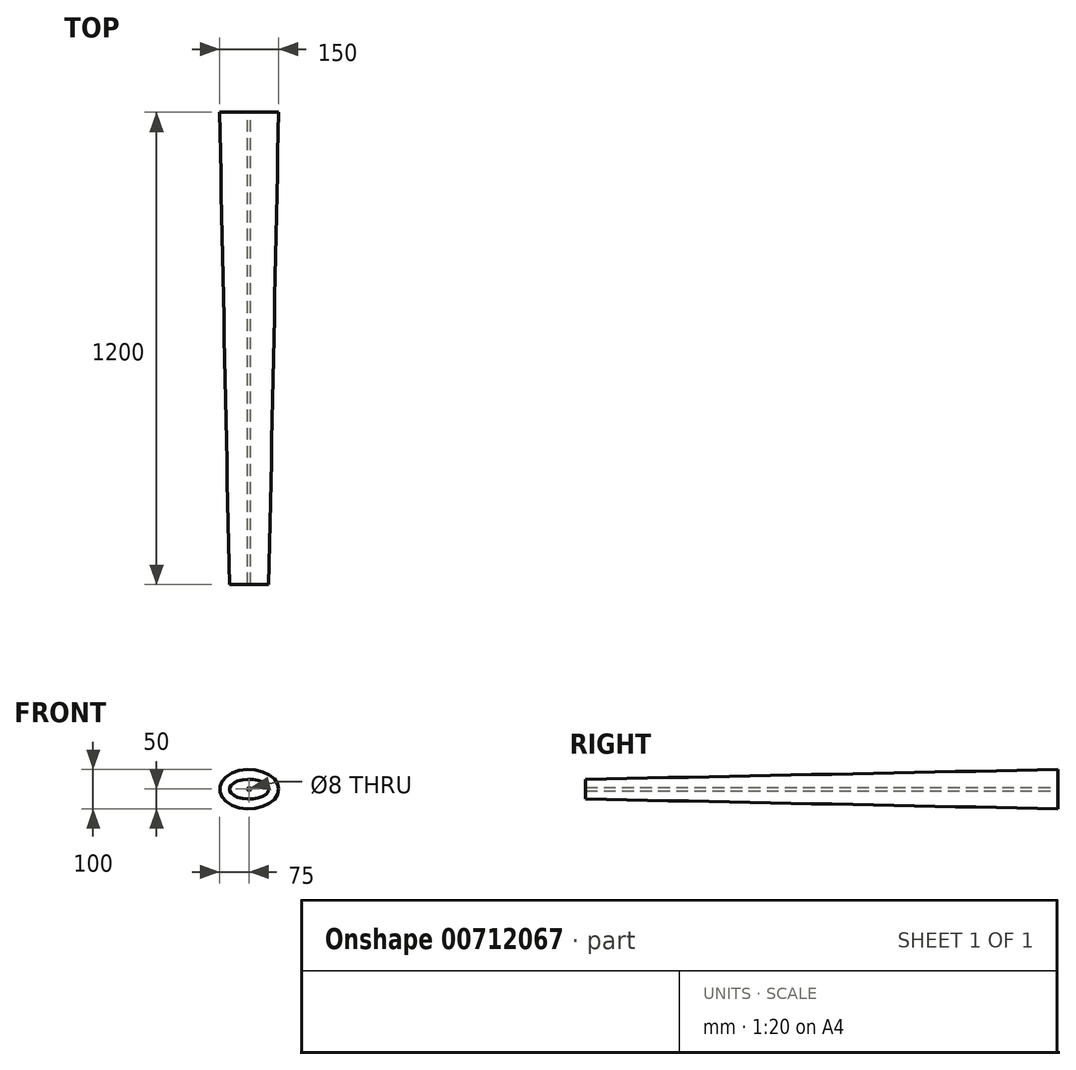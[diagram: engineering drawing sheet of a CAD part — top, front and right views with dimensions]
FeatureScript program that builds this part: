
annotation { "Feature Type Name" : "Feature", "Feature Type Description" : "" }
export const myFeature = defineFeature(function(context is Context, id is Id, definition is map)
    precondition{}
    {
        {
            var Q0;
            Q0=qCreatedBy(makeId("Front.planeOp"),FACE);
            var sketch = newSketch(context, id + "F0", { "sketchPlane" : qUnion([Q0])});
            skEllipse(sketch, "E0", {"center": v(0, 0) * mm, "majorRadius": 75 * mm, "minorRadius": 50 * mm, "majorAxis": v(1, 0)});
            skSolve(sketch);
        }
        {
            var Q0;
            Q0=makeQuery(id+"F0.imprint","IMPRINT",FACE,{"disambiguationData":[TD([[makeQuery(id+"F0.imprint","IMPRINT",EDGE,{"derivedFrom":sQuery(id+"F0.wireOp",EDGE,"E0")}),1.0]])]});
            cPlane(context, id + "F1", {"entities" : qUnion([Q0]), "cplaneType" : CPlaneType.OFFSET, "offset" : 1200 * mm, "width" : 150 * mm, "height" : 150 * mm});
        }
        {
            var Q0;
            Q0=qCreatedBy(id+"F1.planeOp",FACE);
            var sketch = newSketch(context, id + "F2", { "sketchPlane" : qUnion([Q0])});
            skEllipse(sketch, "E1", {"center": v(0, 0) * mm, "majorRadius": 50 * mm, "minorRadius": 25 * mm, "majorAxis": v(1, 0)});
            skSolve(sketch);
        }
        {
            var Q0;
            Q0=makeQuery(id+"F0.imprint","IMPRINT",FACE,{"disambiguationData":[TD([[makeQuery(id+"F0.imprint","IMPRINT",EDGE,{"derivedFrom":sQuery(id+"F0.wireOp",EDGE,"E0")}),1.0]])]});
            var Q1;
            Q1=makeQuery(id+"F2.imprint","IMPRINT",FACE,{"disambiguationData":[TD([[makeQuery(id+"F2.imprint","IMPRINT",EDGE,{"derivedFrom":sQuery(id+"F2.wireOp",EDGE,"E1")}),1.0]])]});
            loft(context, id + "F3", {"sheetProfilesArray" : [{ "sheetProfileEntities" : qUnion([Q0]) }, { "sheetProfileEntities" : qUnion([Q1]) }]});
        }
        {
            var Q0;
            Q0=makeQuery(id+"F3.opLoft","CAP_FACE",FACE,{"disambiguationData":[OSD([makeQuery(id+"F0.imprint","IMPRINT",FACE,{"disambiguationData":[TD([[makeQuery(id+"F0.imprint","IMPRINT",EDGE,{"derivedFrom":sQuery(id+"F0.wireOp",EDGE,"E0")}),1.0]])]})])],"isStart":true});
            var sketch = newSketch(context, id + "F4", { "sketchPlane" : qUnion([Q0])});
            skCircle(sketch, "E2", {"center": v(0, 0) * mm, "radius": 4 * mm});
            skArc(sketch, "E3", {"start": v(-7.42, -3) * mm, "mid": v(-5.66, -5.66) * mm, "end": v(-3, -7.42) * mm});
            skFitSpline(sketch, "E4.0", {"points": [v(-68.8, -4.03) * mm, v(-69.1, 0) * mm, v(-68.8, 4.03) * mm, v(-67.91, 8.04) * mm, v(-66.41, 12.04) * mm, v(-63.6, 17.3) * mm, v(-58.52, 23.65) * mm, v(-50.05, 30.55) * mm, v(-39.5, 36.33) * mm, v(-27.3, 40.69) * mm, v(-13.94, 43.39) * mm, v(0, 44.3) * mm, v(13.94, 43.39) * mm, v(27.3, 40.69) * mm, v(39.5, 36.33) * mm, v(50.05, 30.55) * mm, v(58.52, 23.65) * mm, v(63.6, 17.3) * mm, v(66.41, 12.04) * mm, v(67.91, 8.04) * mm, v(68.8, 4.03) * mm, v(69.1, 0) * mm, v(68.8, -4.03) * mm, v(67.91, -8.04) * mm, v(66.41, -12.04) * mm, v(63.6, -17.3) * mm, v(58.52, -23.65) * mm, v(50.05, -30.55) * mm, v(39.5, -36.33) * mm, v(27.3, -40.69) * mm, v(13.94, -43.39) * mm, v(0, -44.3) * mm, v(-13.94, -43.39) * mm, v(-27.3, -40.69) * mm, v(-39.5, -36.33) * mm, v(-50.05, -30.55) * mm, v(-58.52, -23.65) * mm, v(-63.6, -17.3) * mm, v(-66.41, -12.04) * mm, v(-67.91, -8.04) * mm, v(-68.8, -4.03) * mm, v(-69.1, 0) * mm, v(-68.8, 4.03) * mm]});
            skLineSegment(sketch, "E5", {"start": v(0, 44) * mm, "end": v(0, 8) * mm, "construction": true});
            skLineSegment(sketch, "E6", {"start": v(-69, 0) * mm, "end": v(-8, 0) * mm, "construction": true});
            skLineSegment(sketch, "E7.0", {"start": v(-68.83, -3) * mm, "end": v(-7.42, -3) * mm});
            skLineSegment(sketch, "E8.0", {"start": v(-68.83, 3) * mm, "end": v(-7.42, 3) * mm});
            skLineSegment(sketch, "E9.0", {"start": v(-3, 43.96) * mm, "end": v(-3, 7.42) * mm});
            skLineSegment(sketch, "E10.0", {"start": v(3, 43.96) * mm, "end": v(3, 7.42) * mm});
            skLineSegment(sketch, "E11.MirrorCS", {"start": v(-3, -43.96) * mm, "end": v(-3, -7.42) * mm});
            skLineSegment(sketch, "E12.MirrorCS", {"start": v(3, -43.96) * mm, "end": v(3, -7.42) * mm});
            skLineSegment(sketch, "E13.MirrorCS", {"start": v(68.83, -3) * mm, "end": v(7.42, -3) * mm});
            skLineSegment(sketch, "E14.MirrorCS", {"start": v(68.83, 3) * mm, "end": v(7.42, 3) * mm});
            skArc(sketch, "E15.trimOffspring", {"start": v(7.42, 3) * mm, "mid": v(5.66, 5.66) * mm, "end": v(3, 7.42) * mm});
            skArc(sketch, "E16.trimOffspring", {"start": v(-3, 7.42) * mm, "mid": v(-5.66, 5.66) * mm, "end": v(-7.42, 3) * mm});
            skArc(sketch, "E17.trimOffspring", {"start": v(3, -7.42) * mm, "mid": v(5.66, -5.66) * mm, "end": v(7.42, -3) * mm});
            skFitSpline(sketch, "E18.trimOffspring", {"points": [v(-68.8, -4.03) * mm, v(-69.1, 0) * mm, v(-68.8, 4.03) * mm, v(-67.91, 8.04) * mm, v(-66.41, 12.04) * mm, v(-63.6, 17.3) * mm, v(-58.52, 23.65) * mm, v(-50.05, 30.55) * mm, v(-39.5, 36.33) * mm, v(-27.3, 40.69) * mm, v(-13.94, 43.39) * mm, v(0, 44.3) * mm, v(13.94, 43.39) * mm, v(27.3, 40.69) * mm, v(39.5, 36.33) * mm, v(50.05, 30.55) * mm, v(58.52, 23.65) * mm, v(63.6, 17.3) * mm, v(66.41, 12.04) * mm, v(67.91, 8.04) * mm, v(68.8, 4.03) * mm, v(69.1, 0) * mm, v(68.8, -4.03) * mm, v(67.91, -8.04) * mm, v(66.41, -12.04) * mm, v(63.6, -17.3) * mm, v(58.52, -23.65) * mm, v(50.05, -30.55) * mm, v(39.5, -36.33) * mm, v(27.3, -40.69) * mm, v(13.94, -43.39) * mm, v(0, -44.3) * mm, v(-13.94, -43.39) * mm, v(-27.3, -40.69) * mm, v(-39.5, -36.33) * mm, v(-50.05, -30.55) * mm, v(-58.52, -23.65) * mm, v(-63.6, -17.3) * mm, v(-66.41, -12.04) * mm, v(-67.91, -8.04) * mm, v(-68.8, -4.03) * mm, v(-69.1, 0) * mm, v(-68.8, 4.03) * mm]});
            skFitSpline(sketch, "E19.trimOffspring", {"points": [v(-68.8, -4.03) * mm, v(-69.1, 0) * mm, v(-68.8, 4.03) * mm, v(-67.91, 8.04) * mm, v(-66.41, 12.04) * mm, v(-63.6, 17.3) * mm, v(-58.52, 23.65) * mm, v(-50.05, 30.55) * mm, v(-39.5, 36.33) * mm, v(-27.3, 40.69) * mm, v(-13.94, 43.39) * mm, v(0, 44.3) * mm, v(13.94, 43.39) * mm, v(27.3, 40.69) * mm, v(39.5, 36.33) * mm, v(50.05, 30.55) * mm, v(58.52, 23.65) * mm, v(63.6, 17.3) * mm, v(66.41, 12.04) * mm, v(67.91, 8.04) * mm, v(68.8, 4.03) * mm, v(69.1, 0) * mm, v(68.8, -4.03) * mm, v(67.91, -8.04) * mm, v(66.41, -12.04) * mm, v(63.6, -17.3) * mm, v(58.52, -23.65) * mm, v(50.05, -30.55) * mm, v(39.5, -36.33) * mm, v(27.3, -40.69) * mm, v(13.94, -43.39) * mm, v(0, -44.3) * mm, v(-13.94, -43.39) * mm, v(-27.3, -40.69) * mm, v(-39.5, -36.33) * mm, v(-50.05, -30.55) * mm, v(-58.52, -23.65) * mm, v(-63.6, -17.3) * mm, v(-66.41, -12.04) * mm, v(-67.91, -8.04) * mm, v(-68.8, -4.03) * mm, v(-69.1, 0) * mm, v(-68.8, 4.03) * mm]});
            skFitSpline(sketch, "E20.trimOffspring", {"points": [v(-68.8, -4.03) * mm, v(-69.1, 0) * mm, v(-68.8, 4.03) * mm, v(-67.91, 8.04) * mm, v(-66.41, 12.04) * mm, v(-63.6, 17.3) * mm, v(-58.52, 23.65) * mm, v(-50.05, 30.55) * mm, v(-39.5, 36.33) * mm, v(-27.3, 40.69) * mm, v(-13.94, 43.39) * mm, v(0, 44.3) * mm, v(13.94, 43.39) * mm, v(27.3, 40.69) * mm, v(39.5, 36.33) * mm, v(50.05, 30.55) * mm, v(58.52, 23.65) * mm, v(63.6, 17.3) * mm, v(66.41, 12.04) * mm, v(67.91, 8.04) * mm, v(68.8, 4.03) * mm, v(69.1, 0) * mm, v(68.8, -4.03) * mm, v(67.91, -8.04) * mm, v(66.41, -12.04) * mm, v(63.6, -17.3) * mm, v(58.52, -23.65) * mm, v(50.05, -30.55) * mm, v(39.5, -36.33) * mm, v(27.3, -40.69) * mm, v(13.94, -43.39) * mm, v(0, -44.3) * mm, v(-13.94, -43.39) * mm, v(-27.3, -40.69) * mm, v(-39.5, -36.33) * mm, v(-50.05, -30.55) * mm, v(-58.52, -23.65) * mm, v(-63.6, -17.3) * mm, v(-66.41, -12.04) * mm, v(-67.91, -8.04) * mm, v(-68.8, -4.03) * mm, v(-69.1, 0) * mm, v(-68.8, 4.03) * mm]});
            skSolve(sketch);
        }
        {
            var Q0;
            Q0=makeQuery(id+"F4.imprint","IMPRINT",FACE,{"disambiguationData":[TD([[makeQuery(id+"F4.imprint","IMPRINT",EDGE,{"derivedFrom":sQuery(id+"F4.wireOp",EDGE,"E2")}),1.0]])]});
            var Q1;
            Q1=sQuery(id+"F4.wireOp",EDGE,"E2");
            extrude(context, id + "F5", {"entities" : qUnion([Q0]), "operationType" : NewBodyOperationType.REMOVE, "surfaceEntities" : qUnion([Q1]), "oppositeDirection" : true, "depth" : 1200 * mm, "offsetDistance" : 25 * mm});
        }
    });
